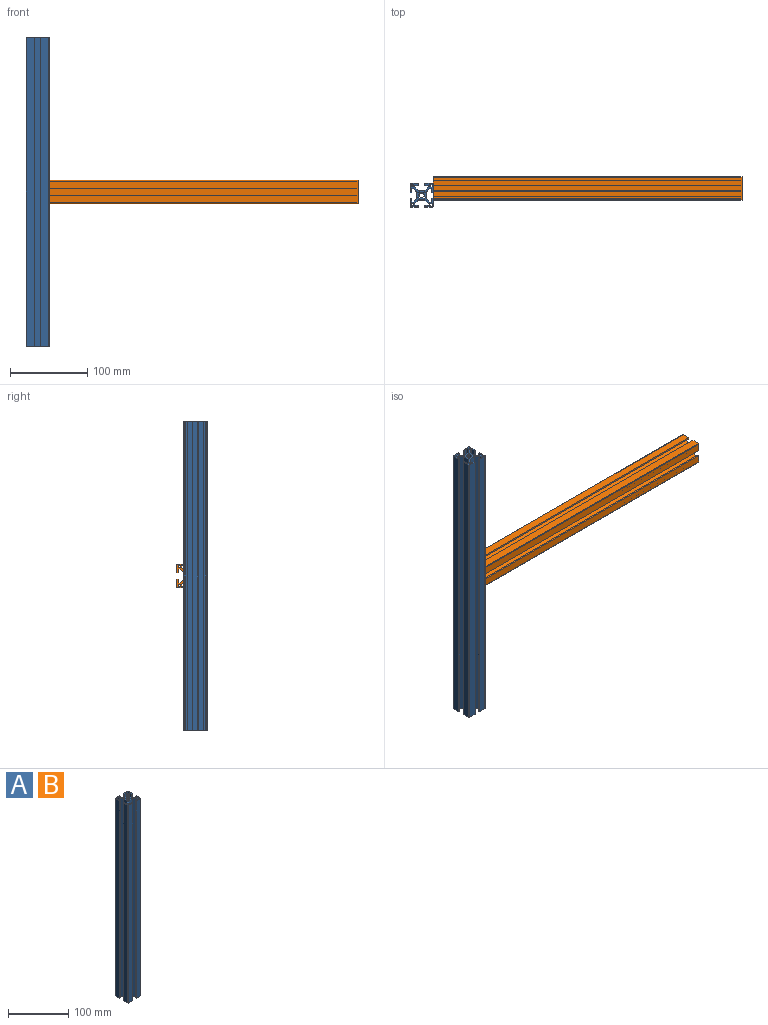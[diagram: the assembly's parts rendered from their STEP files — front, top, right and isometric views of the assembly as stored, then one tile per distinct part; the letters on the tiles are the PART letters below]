
ASSEMBLY  parts=2 mates=1
PART A: 82 faces, bbox 30x30x400 mm
  f0: plane 400x3mm, normal (1,0,0), area 1200mm2, adj f1,f75,f76,f77
  f1: plane 400x3mm, normal (0,-1,0), area 1200mm2, adj f0,f2,f76,f77
  f2: plane 400x3mm, normal (-1,0,0), area 1200mm2, adj f1,f75,f76,f77
  f3: plane 400x1.41mm, normal (0.71,-0.71,0), area 800mm2, adj f4,f70,f76,f77
  f4: plane 400x1.66mm, normal (-0.71,-0.71,0), area 940.2mm2, adj f3,f5,f76,f77
  f5: cylinder r=3.4mm len=400mm, axis (0,0,-1), area 1324.3mm2, adj f4,f6,f76,f77
  f6: plane 400x1.66mm, normal (0.71,-0.71,0), area 940.2mm2, adj f5,f7,f76,f77
  f7: plane 400x1.41mm, normal (-0.71,-0.71,0), area 800mm2, adj f6,f8,f76,f77
  f8: plane 400x1.66mm, normal (-0.71,0.71,0), area 940.2mm2, adj f7,f9,f76,f77
  f9: cylinder r=3.4mm len=400mm, axis (0,0,-1), area 1324.3mm2, adj f8,f10,f76,f77
  f10: plane 400x1.66mm, normal (-0.71,-0.71,0), area 940.2mm2, adj f9,f11,f76,f77
  f11: plane 400x1.41mm, normal (-0.71,0.71,0), area 800mm2, adj f10,f12,f76,f77
  f12: plane 400x1.66mm, normal (0.71,0.71,0), area 940.2mm2, adj f11,f13,f76,f77
  f13: cylinder r=3.4mm len=400mm, axis (0,0,-1), area 1324.3mm2, adj f12,f14,f76,f77
  f14: plane 400x1.66mm, normal (-0.71,0.71,0), area 940.2mm2, adj f13,f15,f76,f77
  f15: plane 400x1.41mm, normal (0.71,0.71,0), area 800mm2, adj f14,f16,f76,f77
  f16: plane 400x1.66mm, normal (0.71,-0.71,0), area 940.2mm2, adj f15,f17,f76,f77
  f17: cylinder r=3.4mm len=400mm, axis (0,0,-1), area 1324.3mm2, adj f16,f70,f76,f77
  f18: plane 400x5mm, normal (1,0,0), area 2000mm2, adj f19,f71,f76,f77
  f19: plane 400x2mm, normal (0,1,0), area 800mm2, adj f18,f20,f76,f77
  f20: plane 400x10mm, normal (-1,0,0), area 4000mm2, adj f19,f76,f77,f78
  f21: plane 400x10mm, normal (0,-1,0), area 4000mm2, adj f22,f76,f77,f78
  f22: plane 400x2mm, normal (1,0,0), area 800mm2, adj f21,f23,f76,f77
  f23: plane 400x5mm, normal (0,1,0), area 2000mm2, adj f22,f24,f76,f77
  f24: plane 400x2.23mm, normal (1,0,0), area 892.9mm2, adj f23,f25,f76,f77
  f25: plane 400x4.77mm, normal (0.71,-0.71,0), area 2697.1mm2, adj f24,f26,f76,f77
  f26: plane 400x8.46mm, normal (0,-1,0), area 3385.8mm2, adj f25,f27,f76,f77
  f27: plane 400x4.77mm, normal (-0.71,-0.71,0), area 2697.1mm2, adj f26,f28,f76,f77
  f28: plane 400x2.23mm, normal (-1,0,0), area 892.9mm2, adj f27,f29,f76,f77
  f29: plane 400x5mm, normal (0,1,0), area 2000mm2, adj f28,f30,f76,f77
  f30: plane 400x2mm, normal (-1,0,0), area 800mm2, adj f29,f31,f76,f77
  f31: plane 400x10mm, normal (0,-1,0), area 4000mm2, adj f30,f76,f77,f79
  f32: plane 400x10mm, normal (1,0,0), area 4000mm2, adj f33,f76,f77,f79
  f33: plane 400x2mm, normal (0,1,0), area 800mm2, adj f32,f34,f76,f77
  f34: plane 400x5mm, normal (-1,0,0), area 2000mm2, adj f33,f35,f76,f77
  f35: plane 400x2.23mm, normal (0,1,0), area 892.9mm2, adj f34,f36,f76,f77
  f36: plane 400x4.77mm, normal (0.71,0.71,0), area 2697.1mm2, adj f35,f37,f76,f77
  f37: plane 400x8.46mm, normal (1,0,0), area 3385.8mm2, adj f36,f38,f76,f77
  f38: plane 400x4.77mm, normal (0.71,-0.71,0), area 2697.1mm2, adj f37,f39,f76,f77
  f39: plane 400x2.23mm, normal (0,-1,0), area 892.9mm2, adj f38,f40,f76,f77
  f40: plane 400x5mm, normal (-1,0,0), area 2000mm2, adj f39,f41,f76,f77
  f41: plane 400x2mm, normal (0,-1,0), area 800mm2, adj f40,f42,f76,f77
  f42: plane 400x10mm, normal (1,0,0), area 4000mm2, adj f41,f76,f77,f80
  f43: plane 400x10mm, normal (0,1,0), area 4000mm2, adj f44,f76,f77,f80
  f44: plane 400x2mm, normal (-1,0,0), area 800mm2, adj f43,f45,f76,f77
  f45: plane 400x5mm, normal (0,-1,0), area 2000mm2, adj f44,f46,f76,f77
  f46: plane 400x2.23mm, normal (-1,0,0), area 892.9mm2, adj f45,f47,f76,f77
  f47: plane 400x4.77mm, normal (-0.71,0.71,0), area 2697.1mm2, adj f46,f48,f76,f77
  f48: plane 400x8.46mm, normal (0,1,0), area 3385.8mm2, adj f47,f49,f76,f77
  f49: plane 400x4.77mm, normal (0.71,0.71,0), area 2697.1mm2, adj f48,f50,f76,f77
  f50: plane 400x2.23mm, normal (1,0,0), area 892.9mm2, adj f49,f51,f76,f77
  f51: plane 400x5mm, normal (0,-1,0), area 2000mm2, adj f50,f52,f76,f77
  f52: plane 400x2mm, normal (1,0,0), area 800mm2, adj f51,f53,f76,f77
  f53: plane 400x10mm, normal (0,1,0), area 4000mm2, adj f52,f76,f77,f81
  f54: plane 400x10mm, normal (-1,0,0), area 4000mm2, adj f55,f76,f77,f81
  f55: plane 400x2mm, normal (0,-1,0), area 800mm2, adj f54,f56,f76,f77
  f56: plane 400x5mm, normal (1,0,0), area 2000mm2, adj f55,f57,f76,f77
  f57: plane 400x2.23mm, normal (0,-1,0), area 892.9mm2, adj f56,f58,f76,f77
  f58: plane 400x4.77mm, normal (-0.71,-0.71,0), area 2697.1mm2, adj f57,f59,f76,f77
  f59: plane 400x8.46mm, normal (-1,0,0), area 3385.8mm2, adj f58,f60,f76,f77
  f60: plane 400x4.77mm, normal (-0.71,0.71,0), area 2697.1mm2, adj f59,f71,f76,f77
  f61: plane 400x3mm, normal (0,-1,0), area 1200mm2, adj f62,f72,f76,f77
  f62: plane 400x3mm, normal (-1,0,0), area 1200mm2, adj f61,f63,f76,f77
  f63: plane 400x3mm, normal (0,1,0), area 1200mm2, adj f62,f72,f76,f77
  f64: plane 400x3mm, normal (1,0,0), area 1200mm2, adj f65,f73,f76,f77
  f65: plane 400x3mm, normal (0,-1,0), area 1200mm2, adj f64,f66,f76,f77
  f66: plane 400x3mm, normal (-1,0,0), area 1200mm2, adj f65,f73,f76,f77
  f67: plane 400x3mm, normal (0,1,0), area 1200mm2, adj f68,f74,f76,f77
  f68: plane 400x3mm, normal (1,0,0), area 1200mm2, adj f67,f69,f76,f77
  f69: plane 400x3mm, normal (0,-1,0), area 1200mm2, adj f68,f74,f76,f77
  f70: plane 400x1.66mm, normal (0.71,0.71,0), area 940.2mm2, adj f3,f17,f76,f77
  f71: plane 400x2.23mm, normal (0,1,0), area 892.9mm2, adj f18,f60,f76,f77
  f72: plane 400x3mm, normal (1,0,0), area 1200mm2, adj f61,f63,f76,f77
  f73: plane 400x3mm, normal (0,1,0), area 1200mm2, adj f64,f66,f76,f77
  f74: plane 400x3mm, normal (-1,0,0), area 1200mm2, adj f67,f69,f76,f77
  f75: plane 400x3mm, normal (0,1,0), area 1200mm2, adj f0,f2,f76,f77
  f76: plane 30x30mm, normal (0,0,1), area 331.8mm2, adj f0,f1,f2,f3,f4,f5,f6,f7
  f77: plane 30x30mm, normal (0,0,-1), area 331.8mm2, adj f0,f1,f2,f3,f4,f5,f6,f7
  f78: cylinder r=1mm len=400mm, axis (0,0,1), area 628.3mm2, adj f20,f21,f76,f77
  f79: cylinder r=1mm len=400mm, axis (0,0,1), area 628.3mm2, adj f31,f32,f76,f77
  f80: cylinder r=1mm len=400mm, axis (0,0,1), area 628.3mm2, adj f42,f43,f76,f77
  f81: cylinder r=1mm len=400mm, axis (0,0,1), area 628.3mm2, adj f53,f54,f76,f77
PART B: same geometry as A
PLACE A t=(-435.65,83.55,302.18)mm
PLACE B rot(axis=(0.71,0,-0.71),180deg) t=(-205.65,122.55,317.18)mm
MATE fastened B.f5 <-> A.f42  axis (-1,0,0) through (-405.65,107.55,302.18)mm
